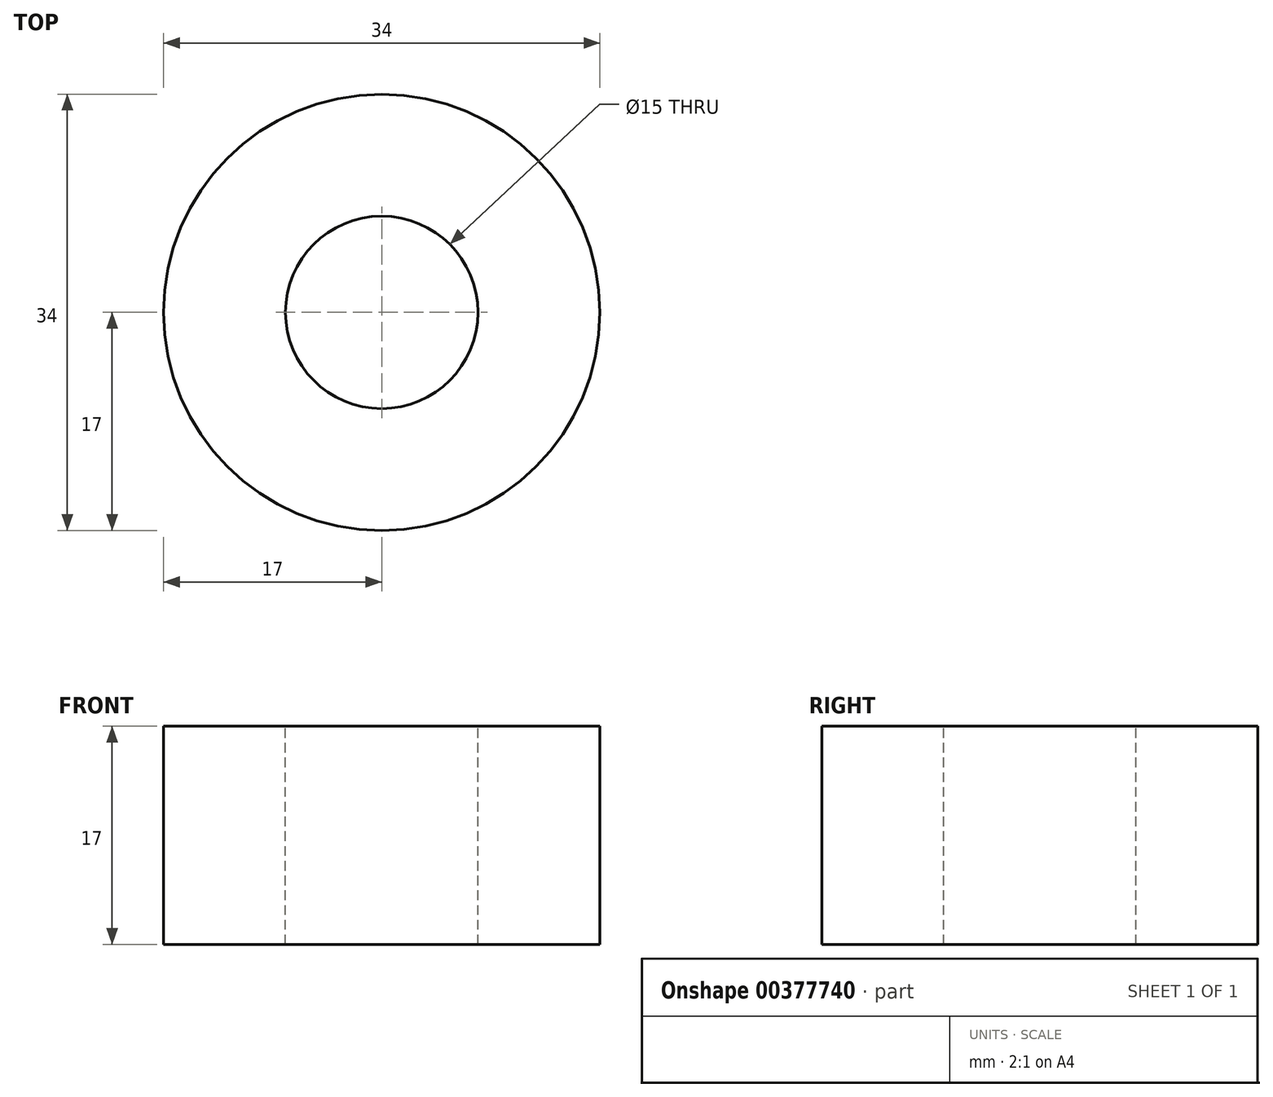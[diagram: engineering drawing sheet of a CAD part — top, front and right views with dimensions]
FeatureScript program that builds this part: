
annotation { "Feature Type Name" : "Feature", "Feature Type Description" : "" }
export const myFeature = defineFeature(function(context is Context, id is Id, definition is map)
    precondition{}
    {
        {
            var Q0;
            Q0=qCreatedBy(makeId("Top.planeOp"),FACE);
            var sketch = newSketch(context, id + "F0", { "sketchPlane" : qUnion([Q0])});
            skCircle(sketch, "E0", {"center": v(0, 0) * mm, "radius": 17 * mm});
            skSolve(sketch);
        }
        {
            var Q0;
            Q0=makeQuery(id+"F0.imprint","IMPRINT",FACE,{"disambiguationData":[TD([[makeQuery(id+"F0.imprint","IMPRINT",EDGE,{"derivedFrom":sQuery(id+"F0.wireOp",EDGE,"E0")}),1.0]])]});
            extrude(context, id + "F1", {"entities" : qUnion([Q0]), "depth" : 17 * mm});
        }
        {
            var Q0;
            Q0=makeQuery(id+"F1.opExtrude","CAP_FACE",FACE,{"disambiguationData":[OSD([sQuery(id+"F0.wireOp",EDGE,"E0")])],"isStart":false});
            var sketch = newSketch(context, id + "F2", { "sketchPlane" : qUnion([Q0])});
            skPoint(sketch, "E1", {"position": v(0, 0) * mm});
            skSolve(sketch);
        }
        {
            var Q0;
            Q0=sQuery(id+"F2.wireOp",VERTEX,"E1");
            var Q1;
            Q1=makeQuery(id+"F1.opExtrude","SWEPT_BODY",BODY,{"disambiguationData":[OSD([sQuery(id+"F0.wireOp",EDGE,"E0")])]});
            hole(context, id + "F3", {"style" : HoleStyle.SIMPLE, "endStyle" : HoleEndStyle.THROUGH, "holeDiameter" : 15 * mm, "isTappedThrough" : true, "tappedDepth" : 12 * mm, "tapClearance" : 3, "locations" : qUnion([Q0]), "scope" : qUnion([Q1])});
        }
    });
